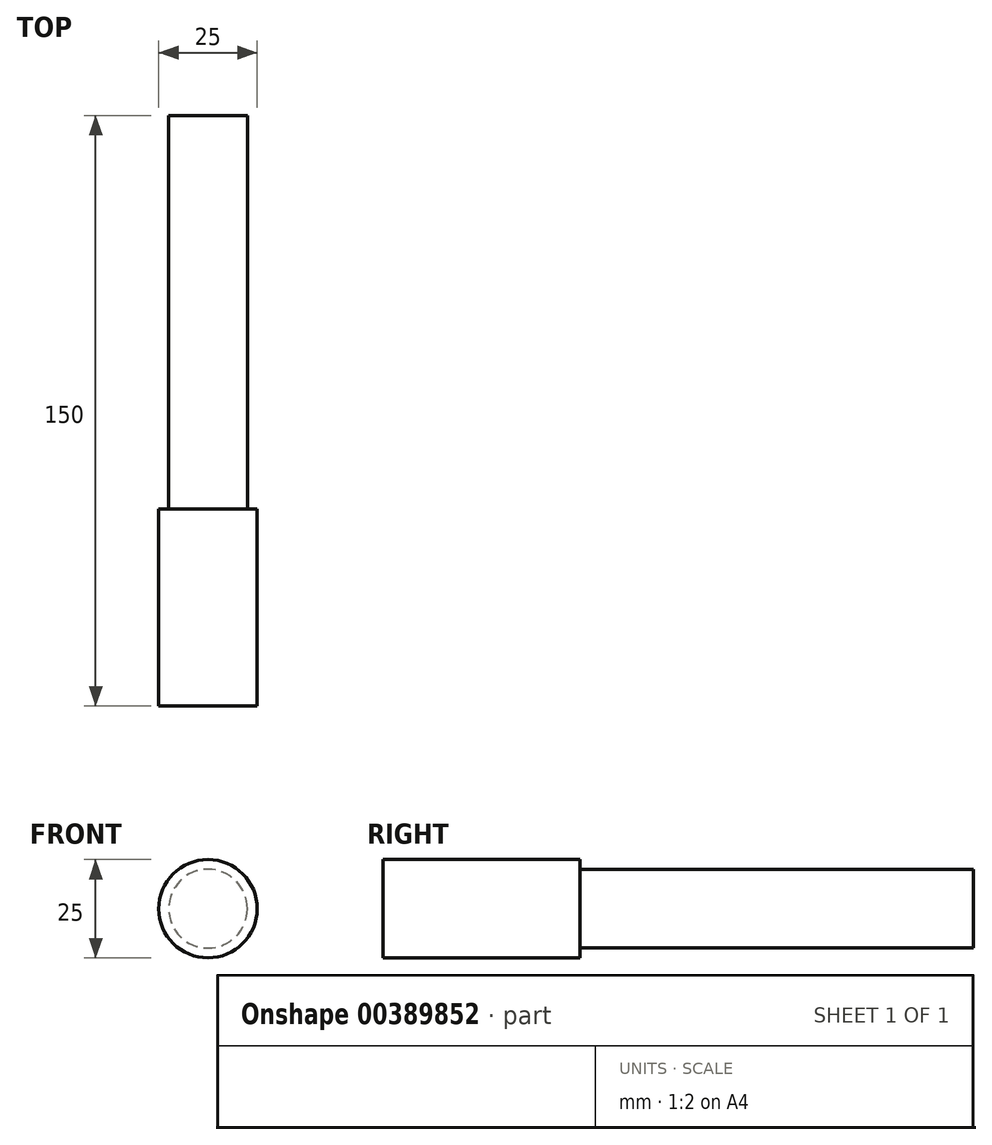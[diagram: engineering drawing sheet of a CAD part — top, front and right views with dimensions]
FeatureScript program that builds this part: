
annotation { "Feature Type Name" : "Feature", "Feature Type Description" : "" }
export const myFeature = defineFeature(function(context is Context, id is Id, definition is map)
    precondition{}
    {
        {
            var Q0;
            Q0=qCreatedBy(makeId("Front.planeOp"),FACE);
            var sketch = newSketch(context, id + "F0", { "sketchPlane" : qUnion([Q0])});
            skCircle(sketch, "E0", {"center": v(0, 0) * mm, "radius": 10 * mm});
            skSolve(sketch);
        }
        {
            var Q0;
            Q0 = qSketchRegion(id + "F0", true);
            var Q1;
            Q1=makeQuery(id+"F0.imprint","IMPRINT",FACE,{"disambiguationData":[TD([[makeQuery(id+"F0.imprint","IMPRINT",EDGE,{"derivedFrom":sQuery(id+"F0.wireOp",EDGE,"E0")}),1.0]])]});
            extrude(context, id + "F1", {"entities" : qUnion([Q0, Q1]), "depth" : 100 * mm});
        }
        {
            var Q0;
            Q0=makeQuery(id+"F1.opExtrude","CAP_FACE",FACE,{"disambiguationData":[OSD([sQuery(id+"F0.wireOp",EDGE,"E0")])],"isStart":false});
            var sketch = newSketch(context, id + "F2", { "sketchPlane" : qUnion([Q0])});
            skCircle(sketch, "E1", {"center": v(0, 0) * mm, "radius": 12.5 * mm});
            skSolve(sketch);
        }
        {
            var Q0;
            Q0=makeQuery(id+"F2.imprint","IMPRINT",FACE,{"disambiguationData":[TD([[makeQuery(id+"F2.imprint","IMPRINT",EDGE,{"derivedFrom":sQuery(id+"F2.wireOp",EDGE,"E1")}),1.0]])]});
            var Q1;
            Q1=makeQuery(id+"F2.imprint","IMPRINT",FACE,{"disambiguationData":[TD([[makeQuery(id+"F2.imprint","IMPRINT",EDGE,{"derivedFrom":sQuery(id+"F2.wireOp",EDGE,"E1")}),1.0]])]});
            var Q2;
            Q2=makeQuery(id+"F2.imprint","IMPRINT",FACE,{"disambiguationData":[TD([[makeQuery(id+"F2.imprint","IMPRINT",EDGE,{"derivedFrom":makeQuery(id+"F1.opExtrude","CAP_EDGE",EDGE,{"disambiguationData":[OSD([sQuery(id+"F0.wireOp",EDGE,"E0")])],"isStart":false})}),1.0]])]});
            extrude(context, id + "F3", {"entities" : qUnion([Q0, Q1, Q2]), "operationType" : NewBodyOperationType.ADD, "depth" : 50 * mm});
        }
    });
